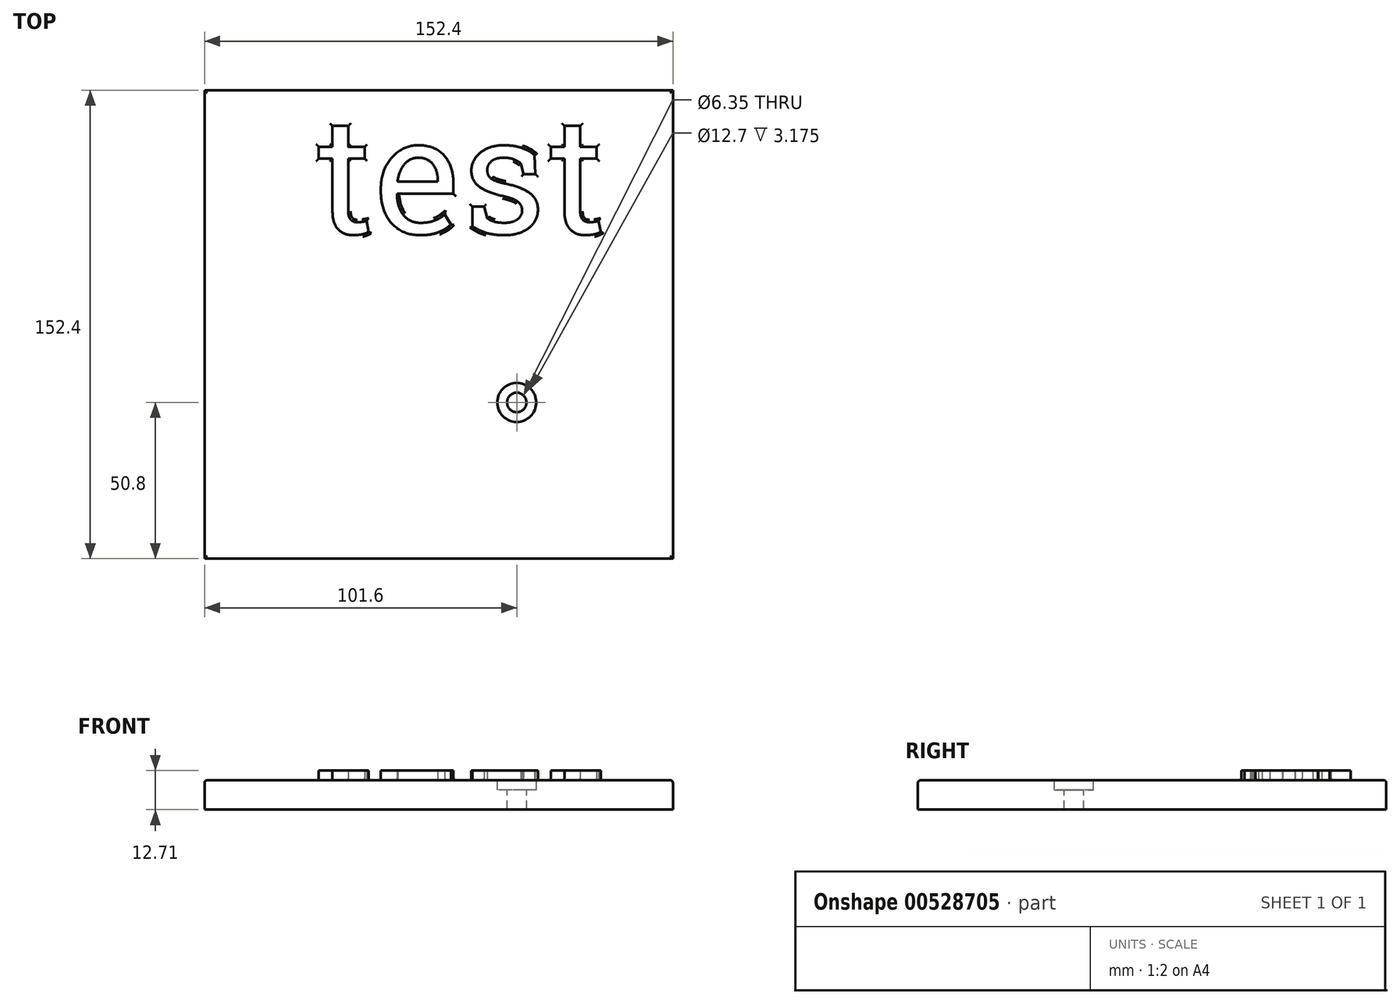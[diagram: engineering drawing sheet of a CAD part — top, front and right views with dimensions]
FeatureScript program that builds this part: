
annotation { "Feature Type Name" : "Feature", "Feature Type Description" : "" }
export const myFeature = defineFeature(function(context is Context, id is Id, definition is map)
    precondition{}
    {
        {
            var Q0;
            Q0=qCreatedBy(makeId("Top.planeOp"),FACE);
            var sketch = newSketch(context, id + "F0", { "sketchPlane" : qUnion([Q0])});
            skLineSegment(sketch, "E0.bottom", {"start": v(0, 0) * mm, "end": v(152.4, 0) * mm});
            skLineSegment(sketch, "E0.top", {"start": v(0, 152.4) * mm, "end": v(152.4, 152.4) * mm});
            skLineSegment(sketch, "E0.left", {"start": v(0, 0) * mm, "end": v(0, 152.4) * mm});
            skLineSegment(sketch, "E0.right", {"start": v(152.4, 0) * mm, "end": v(152.4, 152.4) * mm});
            skSolve(sketch);
        }
        {
            var Q0;
            Q0=makeQuery(id+"F0.imprint","IMPRINT",FACE,{"disambiguationData":[TD([[makeQuery(id+"F0.imprint","IMPRINT",EDGE,{"derivedFrom":sQuery(id+"F0.wireOp",EDGE,"E0.bottom")}),1.0]])]});
            extrude(context, id + "F1", {"entities" : qUnion([Q0]), "oppositeDirection" : true, "depth" : 9.52 * mm, "offsetDistance" : 25.4 * mm});
        }
        {
            var Q0;
            Q0=makeQuery(id+"F1.opExtrude","CAP_FACE",FACE,{"disambiguationData":[OSD([sQuery(id+"F0.wireOp",EDGE,"E0.bottom"),sQuery(id+"F0.wireOp",EDGE,"E0.top"),sQuery(id+"F0.wireOp",EDGE,"E0.left"),sQuery(id+"F0.wireOp",EDGE,"E0.right")])],"isStart":true});
            var sketch = newSketch(context, id + "F2", { "sketchPlane" : qUnion([Q0])});
            skText(sketch, "E1", { "text": "test", "fontName": "RobotoSlab-Regular.ttf"});
            const initialGuessF2  = {"E1": [0.03549, 0.10578, 1, 0, 0.03844]};
            skSetInitialGuess(sketch, initialGuessF2);
            skSolve(sketch);
        }
        {
            var Q0;
            Q0=makeQuery(id+"F2.imprint","IMPRINT",FACE,{"disambiguationData":[TD([[makeQuery(id+"F2.imprint","IMPRINT",EDGE,{"derivedFrom":sQuery(id+"F2.wireOp",EDGE,"E1.sketch_text.stroke-0")}),-1.0]])]});
            var Q1;
            {var subQ4=sQuery(id+"F2.wireOp",EDGE,"E1.sketch_text.stroke-22");Q1=makeQuery(id+"F2.imprint","IMPRINT",FACE,{"disambiguationData":[TD([[makeQuery(id+"F2.imprint","IMPRINT",EDGE,{"derivedFrom":subQ4}),-1.0]])]});}
            var Q2;
            Q2=makeQuery(id+"F2.imprint","IMPRINT",FACE,{"disambiguationData":[TD([[makeQuery(id+"F2.imprint","IMPRINT",EDGE,{"derivedFrom":sQuery(id+"F2.wireOp",EDGE,"E1.sketch_text.stroke-44")}),-1.0]])]});
            var Q3;
            Q3=makeQuery(id+"F2.imprint","IMPRINT",FACE,{"disambiguationData":[TD([[makeQuery(id+"F2.imprint","IMPRINT",EDGE,{"derivedFrom":sQuery(id+"F2.wireOp",EDGE,"E1.sketch_text.stroke-74")}),-1.0]])]});
            extrude(context, id + "F3", {"entities" : qUnion([Q0, Q1, Q2, Q3]), "operationType" : NewBodyOperationType.ADD, "depth" : 3.17 * mm, "offsetDistance" : 25.4 * mm});
        }
        {
            var Q0;
            {var subQ0=sQuery(id+"F0.wireOp",EDGE,"E0.top");var subQ6=sQuery(id+"F0.wireOp",EDGE,"E0.bottom");var subQ7=sQuery(id+"F0.wireOp",EDGE,"E0.right");var subQ9=sQuery(id+"F0.wireOp",EDGE,"E0.left");var subQ11=makeQuery(id+"F1.opExtrude","CAP_FACE",FACE,{"disambiguationData":[OSD([subQ6,subQ0,subQ9,subQ7])],"isStart":true});Q0=makeQuery(id+"F3.boolean.opBoolean","SPLIT",FACE,{"disambiguationData":[TD([makeQuery(id+"F1.opExtrude","SWEPT_FACE",FACE,{"disambiguationData":[OSD([subQ6])]})])],"derivedFrom":subQ11});}
            fillet(context, id + "F4", {"entities" : qUnion([Q0]), "radius" : 0.8 * mm, "tangentPropagation" : true, "allowEdgeOverflow" : false});
        }
        {
            var Q0;
            {var subQ0=sQuery(id+"F0.wireOp",EDGE,"E0.left");var subQ1=sQuery(id+"F0.wireOp",EDGE,"E0.bottom");var subQ2=sQuery(id+"F0.wireOp",EDGE,"E0.right");var subQ3=sQuery(id+"F0.wireOp",EDGE,"E0.top");Q0=makeQuery(id+"F3.boolean.opBoolean","SPLIT",FACE,{"disambiguationData":[TD([makeQuery(id+"F1.opExtrude","SWEPT_FACE",FACE,{"disambiguationData":[OSD([subQ1])]})])],"derivedFrom":makeQuery(id+"F1.opExtrude","CAP_FACE",FACE,{"disambiguationData":[OSD([subQ1,subQ3,subQ0,subQ2])],"isStart":true})});}
            var sketch = newSketch(context, id + "F5", { "sketchPlane" : qUnion([Q0])});
            skPoint(sketch, "E2", {"position": v(101.6, 50.8) * mm});
            skSolve(sketch);
        }
        {
            var Q0;
            Q0=sQuery(id+"F5.wireOp",VERTEX,"E2");
            var Q1;
            Q1=makeQuery(id+"F1.opExtrude","SWEPT_BODY",BODY,{"disambiguationData":[OSD([sQuery(id+"F0.wireOp",EDGE,"E0.bottom"),sQuery(id+"F0.wireOp",EDGE,"E0.top"),sQuery(id+"F0.wireOp",EDGE,"E0.left"),sQuery(id+"F0.wireOp",EDGE,"E0.right")])]});
            hole(context, id + "F6", {"style" : HoleStyle.C_BORE, "endStyle" : HoleEndStyle.THROUGH, "holeDiameter" : 6.35 * mm, "cBoreDiameter" : 12.7 * mm, "cBoreDepth" : 3.17 * mm, "isTappedThrough" : true, "tappedDepth" : 12.7 * mm, "tapClearance" : 3, "locations" : qUnion([Q0]), "scope" : qUnion([Q1])});
        }
    });
